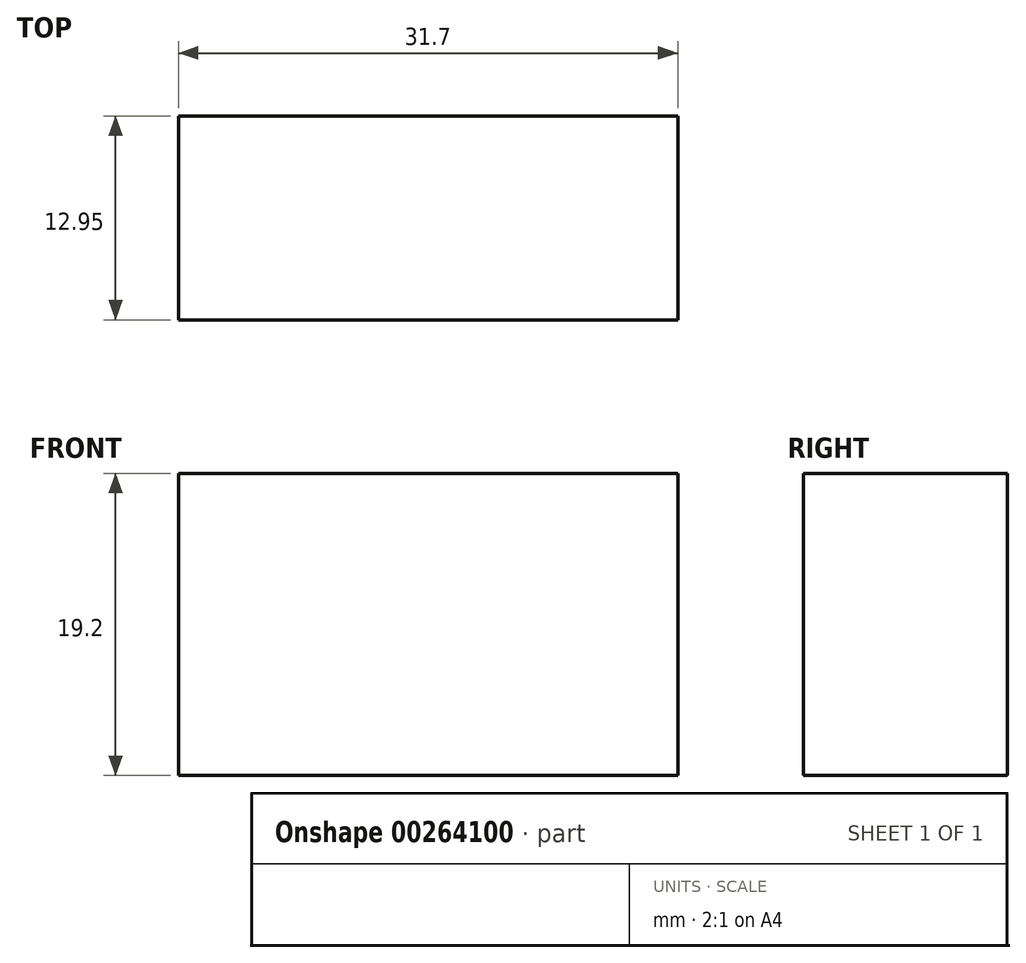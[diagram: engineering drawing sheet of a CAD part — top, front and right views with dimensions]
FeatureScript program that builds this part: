
annotation { "Feature Type Name" : "Feature", "Feature Type Description" : "" }
export const myFeature = defineFeature(function(context is Context, id is Id, definition is map)
    precondition{}
    {
        {
            var Q0;
            Q0=qCreatedBy(makeId("Front.planeOp"),FACE);
            var sketch = newSketch(context, id + "F0", { "sketchPlane" : qUnion([Q0])});
            skLineSegment(sketch, "E0.bottom", {"start": v(-15.85, 9.6) * mm, "end": v(15.85, 9.6) * mm});
            skLineSegment(sketch, "E0.top", {"start": v(-15.85, -9.6) * mm, "end": v(15.85, -9.6) * mm});
            skLineSegment(sketch, "E0.left", {"start": v(-15.85, 9.6) * mm, "end": v(-15.85, -9.6) * mm});
            skLineSegment(sketch, "E0.right", {"start": v(15.85, 9.6) * mm, "end": v(15.85, -9.6) * mm});
            skPoint(sketch, "E0.middle", {"position": v(0, 0) * mm});
            skCircle(sketch, "E1", {"center": v(-9.14, 0) * mm, "radius": 4.52 * mm});
            skCircle(sketch, "E2", {"center": v(8.84, 0) * mm, "radius": 4.88 * mm});
            skSolve(sketch);
        }
        {
            var Q0;
            Q0=makeQuery(id+"F0.imprint","IMPRINT",FACE,{"disambiguationData":[TD([[makeQuery(id+"F0.imprint","IMPRINT",EDGE,{"derivedFrom":sQuery(id+"F0.wireOp",EDGE,"E0.bottom")}),-1.0]])]});
            var Q1;
            Q1=makeQuery(id+"F0.imprint","IMPRINT",FACE,{"disambiguationData":[TD([[makeQuery(id+"F0.imprint","IMPRINT",EDGE,{"derivedFrom":sQuery(id+"F0.wireOp",EDGE,"E1")}),1.0]])]});
            var Q2;
            Q2=makeQuery(id+"F0.imprint","IMPRINT",FACE,{"disambiguationData":[TD([[makeQuery(id+"F0.imprint","IMPRINT",EDGE,{"derivedFrom":sQuery(id+"F0.wireOp",EDGE,"E2")}),1.0]])]});
            extrude(context, id + "F1", {"entities" : qUnion([Q0, Q1, Q2]), "depth" : 12.95 * mm});
        }
        {
            var Q0;
            Q0=sQuery(id+"F0.wireOp",EDGE,"E1");
            var Q1;
            Q1=sQuery(id+"F0.wireOp",EDGE,"E2");
            extrude(context, id + "F2", {"bodyType" : ToolBodyType.SURFACE, "surfaceEntities" : qUnion([Q0, Q1]), "oppositeDirection" : true, "depth" : 7.62 * mm});
        }
    });
